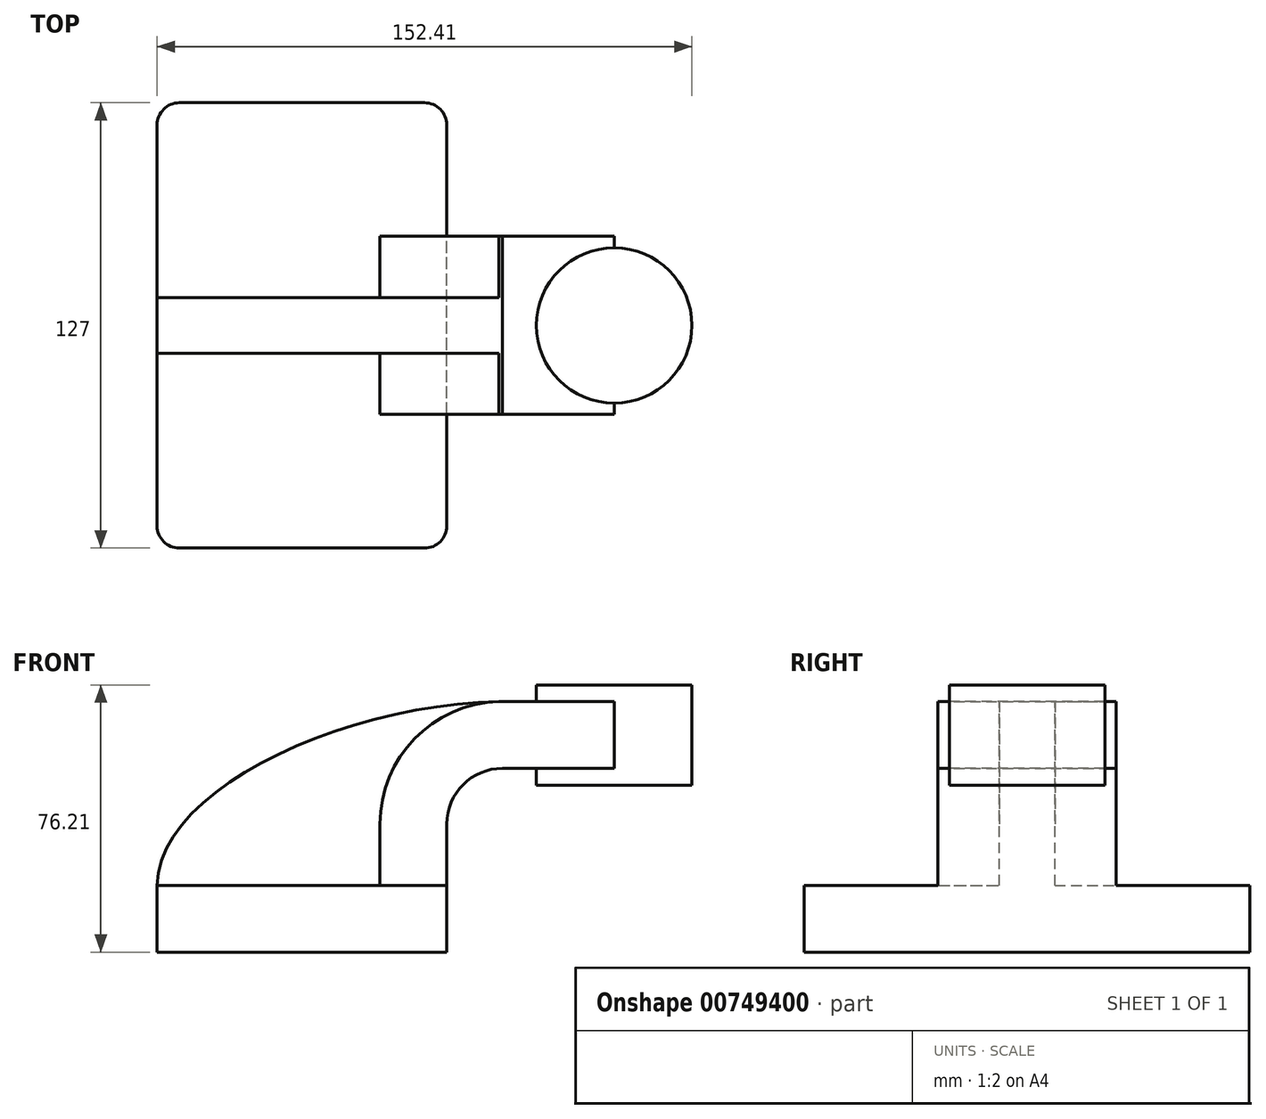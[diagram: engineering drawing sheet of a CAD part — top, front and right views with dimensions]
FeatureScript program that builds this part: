
annotation { "Feature Type Name" : "Feature", "Feature Type Description" : "" }
export const myFeature = defineFeature(function(context is Context, id is Id, definition is map)
    precondition{}
    {
        {
            var Q0;
            Q0=qCreatedBy(makeId("Front.planeOp"),FACE);
            var sketch = newSketch(context, id + "F0", { "sketchPlane" : qUnion([Q0])});
            skLineSegment(sketch, "E0.bottom", {"start": v(-41.28, -9.53) * mm, "end": v(41.28, -9.53) * mm});
            skLineSegment(sketch, "E0.top", {"start": v(-41.28, 9.53) * mm, "end": v(41.28, 9.53) * mm});
            skLineSegment(sketch, "E0.left", {"start": v(-41.28, -9.53) * mm, "end": v(-41.28, 9.53) * mm});
            skLineSegment(sketch, "E0.right", {"start": v(41.28, -9.53) * mm, "end": v(41.28, 9.53) * mm});
            skPoint(sketch, "E0.middle", {"position": v(0, 0) * mm});
            skLineSegment(sketch, "E1.bottom", {"start": v(111.12, 38.1) * mm, "end": v(60.32, 38.1) * mm});
            skLineSegment(sketch, "E1.top", {"start": v(111.12, 66.67) * mm, "end": v(60.32, 66.67) * mm});
            skLineSegment(sketch, "E1.left", {"start": v(111.12, 38.1) * mm, "end": v(111.12, 66.67) * mm});
            skLineSegment(sketch, "E1.right", {"start": v(60.32, 38.1) * mm, "end": v(60.32, 66.67) * mm});
            skPoint(sketch, "E1.middle", {"position": v(85.72, 52.39) * mm});
            skLineSegment(sketch, "E2", {"start": v(41.27, 9.53) * mm, "end": v(41.27, 27) * mm});
            skArc(sketch, "E3", {"start": v(41.27, 27) * mm, "mid": v(45.92, 38.23) * mm, "end": v(57.15, 42.88) * mm});
            skLineSegment(sketch, "E4", {"start": v(57.15, 42.88) * mm, "end": v(88.98, 42.88) * mm});
            skLineSegment(sketch, "E5.0", {"start": v(57.15, 61.93) * mm, "end": v(88.98, 61.93) * mm});
            skArc(sketch, "E5.1", {"start": v(22.22, 27) * mm, "mid": v(32.45, 51.7) * mm, "end": v(57.15, 61.93) * mm});
            skLineSegment(sketch, "E5.2", {"start": v(22.22, 9.53) * mm, "end": v(22.22, 27) * mm});
            skLineSegment(sketch, "E6", {"start": v(88.98, 66.67) * mm, "end": v(88.98, 38.1) * mm});
            skFitSpline(sketch, "E7", {"points": [v(-41.28, 9.53) * mm, v(57.15, 61.93) * mm], "startDerivative": vector(0.68, 82.36) * mm, "endDerivative": vector(134.51, 1.43) * mm});
            skSolve(sketch);
        }
        {
            var Q0;
            Q0=makeQuery(id+"F0.imprint","IMPRINT",FACE,{"disambiguationData":[TD([[makeQuery(id+"F0.imprint","IMPRINT",EDGE,{"derivedFrom":sQuery(id+"F0.wireOp",EDGE,"E0.bottom")}),1.0]])]});
            extrude(context, id + "F1", {"entities" : qUnion([Q0]), "endBound" : BoundingType.SYMMETRIC, "depth" : 127 * mm, "offsetDistance" : 25.4 * mm});
        }
        {
            var Q0;
            {var subQ1=sQuery(id+"F0.wireOp",EDGE,"E2");Q0=makeQuery(id+"F0.imprint","IMPRINT",FACE,{"disambiguationData":[TD([[makeQuery(id+"F0.imprint","IMPRINT",EDGE,{"derivedFrom":subQ1}),1.0]])]});}
            var Q1;
            {var subQ0=sQuery(id+"F0.wireOp",EDGE,"E4");var subQ1=sQuery(id+"F0.wireOp",EDGE,"E1.right");var subQ2=makeQuery(id+"F0.imprint","INTERSECT",VERTEX,{"derivedFrom":[subQ1,subQ0]});Q1=makeQuery(id+"F0.imprint","IMPRINT",FACE,{"disambiguationData":[TD([[makeQuery(id+"F0.imprint","IMPRINT",EDGE,{"disambiguationData":[TD([[subQ2,-1.0]])],"derivedFrom":subQ1}),-1.0]])]});}
            extrude(context, id + "F2", {"entities" : qUnion([Q0, Q1]), "operationType" : NewBodyOperationType.ADD, "endBound" : BoundingType.SYMMETRIC, "depth" : 50.8 * mm, "offsetDistance" : 25.4 * mm});
        }
        {
            var Q0;
            {var subQ3=sQuery(id+"F0.wireOp",EDGE,"E5.2");Q0=makeQuery(id+"F0.imprint","IMPRINT",FACE,{"disambiguationData":[TD([[makeQuery(id+"F0.imprint","IMPRINT",EDGE,{"derivedFrom":subQ3}),1.0]])]});}
            extrude(context, id + "F3", {"entities" : qUnion([Q0]), "operationType" : NewBodyOperationType.ADD, "endBound" : BoundingType.SYMMETRIC, "depth" : 15.88 * mm, "offsetDistance" : 25.4 * mm});
        }
        {
            var Q0;
            {var subQ0=sQuery(id+"F0.wireOp",EDGE,"E1.left");Q0=makeQuery(id+"F0.imprint","IMPRINT",FACE,{"disambiguationData":[TD([[makeQuery(id+"F0.imprint","IMPRINT",EDGE,{"derivedFrom":subQ0}),1.0]])]});}
            var Q1;
            Q1=sQuery(id+"F0.wireOp",EDGE,"E6");
            revolve(context, id + "F4", {"operationType" : NewBodyOperationType.ADD, "surfaceOperationType" : NewSurfaceOperationType.NEW, "entities" : qUnion([Q0]), "axis" : qUnion([Q1]), "revolveType" : RevolveType.FULL});
        }
        {
            var Q0;
            Q0=makeQuery(id+"F1.opExtrude","CAP_EDGE",EDGE,{"disambiguationData":[OSD([sQuery(id+"F0.wireOp",EDGE,"E0.left")])],"isStart":false});
            var Q1;
            Q1=makeQuery(id+"F1.opExtrude","CAP_EDGE",EDGE,{"disambiguationData":[OSD([sQuery(id+"F0.wireOp",EDGE,"E0.right")])],"isStart":false});
            var Q2;
            Q2=makeQuery(id+"F1.opExtrude","CAP_EDGE",EDGE,{"disambiguationData":[OSD([sQuery(id+"F0.wireOp",EDGE,"E0.left")])],"isStart":true});
            var Q3;
            Q3=makeQuery(id+"F1.opExtrude","CAP_EDGE",EDGE,{"disambiguationData":[OSD([sQuery(id+"F0.wireOp",EDGE,"E0.right")])],"isStart":true});
            fillet(context, id + "F5", {"entities" : qUnion([Q0, Q1, Q2, Q3]), "radius" : 6.35 * mm, "tangentPropagation" : true, "allowEdgeOverflow" : false});
        }
    });
